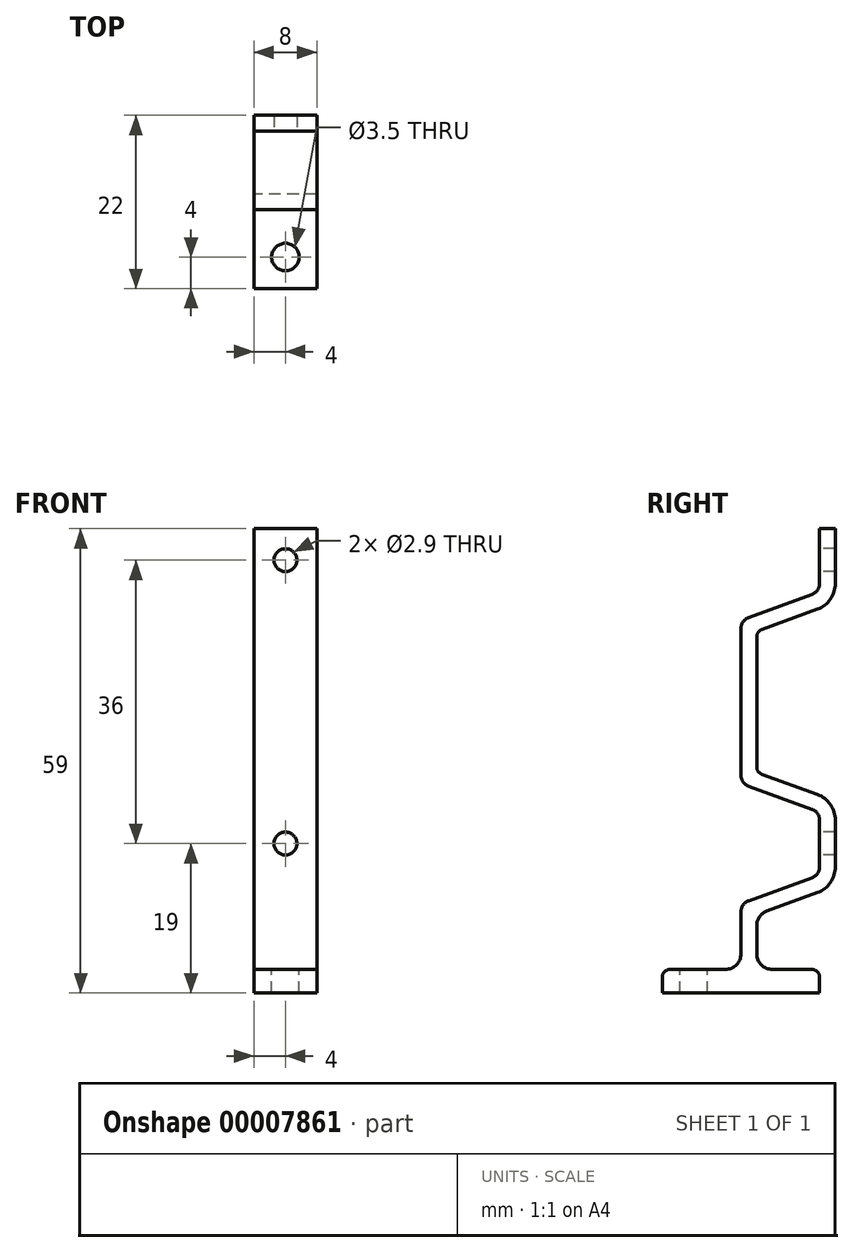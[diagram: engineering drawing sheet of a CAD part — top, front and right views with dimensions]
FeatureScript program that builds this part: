
annotation { "Feature Type Name" : "Feature", "Feature Type Description" : "" }
export const myFeature = defineFeature(function(context is Context, id is Id, definition is map)
    precondition{}
    {
        {
            var Q0;
            Q0=qCreatedBy(makeId("Front.planeOp"),FACE);
            var sketch = newSketch(context, id + "F0", { "sketchPlane" : qUnion([Q0])});
            skPoint(sketch, "E0.rect.middle", {"position": v(0, 0) * mm});
            skCircle(sketch, "E1", {"center": v(0, 52) * mm, "radius": 1.45 * mm});
            skCircle(sketch, "E2", {"center": v(0, 16) * mm, "radius": 1.45 * mm});
            skSolve(sketch);
        }
        {
            var Q0;
            Q0=qCreatedBy(makeId("Right.planeOp"),FACE);
            var sketch = newSketch(context, id + "F1", { "sketchPlane" : qUnion([Q0])});
            skLineSegment(sketch, "E3", {"start": v(0, 2) * mm, "end": v(0, 7.3) * mm});
            skLineSegment(sketch, "E4", {"start": v(0.99, 8.72) * mm, "end": v(9.01, 11.64) * mm});
            skLineSegment(sketch, "E5", {"start": v(10, 13.05) * mm, "end": v(10, 18.95) * mm});
            skLineSegment(sketch, "E6", {"start": v(9.01, 20.36) * mm, "end": v(0.99, 23.28) * mm});
            skLineSegment(sketch, "E7", {"start": v(0, 24.7) * mm, "end": v(0, 43.3) * mm});
            skLineSegment(sketch, "E8", {"start": v(0.99, 44.72) * mm, "end": v(9.01, 47.64) * mm});
            skLineSegment(sketch, "E9", {"start": v(10, 49.05) * mm, "end": v(10, 56) * mm});
            skLineSegment(sketch, "E10", {"start": v(10, 16) * mm, "end": v(0, 16) * mm, "construction": true});
            skLineSegment(sketch, "E11", {"start": v(10, 52) * mm, "end": v(0, 52) * mm, "construction": true});
            skLineSegment(sketch, "E12.bottom", {"start": v(-9, 0) * mm, "end": v(-2, 0) * mm});
            skLineSegment(sketch, "E12.top", {"start": v(-10, -3) * mm, "end": v(10, -3) * mm});
            skLineSegment(sketch, "E12.left", {"start": v(-10, -1) * mm, "end": v(-10, -3) * mm});
            skLineSegment(sketch, "E12.right", {"start": v(10, -1) * mm, "end": v(10, -3) * mm});
            skPoint(sketch, "E13.visualSharp", {"position": v(10, 48) * mm});
            skArc(sketch, "E13.filletArc", {"start": v(9.01, 47.64) * mm, "mid": v(9.73, 48.19) * mm, "end": v(10, 49.05) * mm});
            skPoint(sketch, "E14.visualSharp", {"position": v(0, 44.36) * mm});
            skArc(sketch, "E14.filletArc", {"start": v(0.99, 44.72) * mm, "mid": v(0.27, 44.17) * mm, "end": v(0, 43.3) * mm});
            skPoint(sketch, "E15.visualSharp", {"position": v(0, 23.64) * mm});
            skArc(sketch, "E15.filletArc", {"start": v(0, 24.7) * mm, "mid": v(0.27, 23.83) * mm, "end": v(0.99, 23.28) * mm});
            skPoint(sketch, "E16.visualSharp", {"position": v(10, 20) * mm});
            skArc(sketch, "E16.filletArc", {"start": v(10, 18.95) * mm, "mid": v(9.73, 19.81) * mm, "end": v(9.01, 20.36) * mm});
            skPoint(sketch, "E17.visualSharp", {"position": v(10, 12) * mm});
            skArc(sketch, "E17.filletArc", {"start": v(9.01, 11.64) * mm, "mid": v(9.73, 12.19) * mm, "end": v(10, 13.05) * mm});
            skPoint(sketch, "E18.visualSharp", {"position": v(0, 8.36) * mm});
            skArc(sketch, "E18.filletArc", {"start": v(0.99, 8.72) * mm, "mid": v(0.27, 8.17) * mm, "end": v(0, 7.3) * mm});
            skLineSegment(sketch, "E19.0", {"start": v(12, 49.05) * mm, "end": v(12, 56) * mm});
            skArc(sketch, "E19.1", {"start": v(9.7, 45.76) * mm, "mid": v(11.37, 47.04) * mm, "end": v(12, 49.05) * mm});
            skLineSegment(sketch, "E19.2", {"start": v(2.66, 43.2) * mm, "end": v(9.7, 45.76) * mm});
            skLineSegment(sketch, "E19.3", {"start": v(2, 25.74) * mm, "end": v(2, 42.26) * mm});
            skLineSegment(sketch, "E19.4", {"start": v(9.7, 22.24) * mm, "end": v(2.66, 24.8) * mm});
            skArc(sketch, "E19.5", {"start": v(12, 18.95) * mm, "mid": v(11.37, 20.96) * mm, "end": v(9.7, 22.24) * mm});
            skLineSegment(sketch, "E19.6", {"start": v(12, 13.05) * mm, "end": v(12, 18.95) * mm});
            skArc(sketch, "E19.7", {"start": v(9.7, 9.76) * mm, "mid": v(11.37, 11.04) * mm, "end": v(12, 13.05) * mm});
            skLineSegment(sketch, "E19.8", {"start": v(3.32, 7.44) * mm, "end": v(9.7, 9.76) * mm});
            skLineSegment(sketch, "E19.9", {"start": v(2, 2) * mm, "end": v(2, 5.56) * mm});
            skLineSegment(sketch, "E20", {"start": v(10, 56) * mm, "end": v(12, 56) * mm});
            skLineSegment(sketch, "E21.trimOffspring", {"start": v(4, 0) * mm, "end": v(9, 0) * mm});
            skPoint(sketch, "E22.visualSharp", {"position": v(0, 0) * mm});
            skArc(sketch, "E22.filletArc", {"start": v(-2, 0) * mm, "mid": v(-0.59, 0.59) * mm, "end": v(0, 2) * mm});
            skPoint(sketch, "E23.visualSharp", {"position": v(2, 0) * mm});
            skArc(sketch, "E23.filletArc", {"start": v(2, 2) * mm, "mid": v(2.59, 0.59) * mm, "end": v(4, 0) * mm});
            skPoint(sketch, "E24.visualSharp", {"position": v(2, 6.96) * mm});
            skArc(sketch, "E24.filletArc", {"start": v(3.32, 7.44) * mm, "mid": v(2.36, 6.7) * mm, "end": v(2, 5.56) * mm});
            skPoint(sketch, "E25.visualSharp", {"position": v(2, 25.04) * mm});
            skArc(sketch, "E25.filletArc", {"start": v(2, 25.74) * mm, "mid": v(2.18, 25.17) * mm, "end": v(2.66, 24.8) * mm});
            skPoint(sketch, "E26.visualSharp", {"position": v(2, 42.96) * mm});
            skArc(sketch, "E26.filletArc", {"start": v(2.66, 43.2) * mm, "mid": v(2.18, 42.83) * mm, "end": v(2, 42.26) * mm});
            skPoint(sketch, "E27.visualSharp", {"position": v(-10, 0) * mm});
            skArc(sketch, "E27.filletArc", {"start": v(-9, 0) * mm, "mid": v(-9.7, -0.3) * mm, "end": v(-10, -1) * mm});
            skPoint(sketch, "E28.visualSharp", {"position": v(10, 0) * mm});
            skArc(sketch, "E28.filletArc", {"start": v(10, -1) * mm, "mid": v(9.7, -0.3) * mm, "end": v(9, 0) * mm});
            skSolve(sketch);
        }
        {
            var Q0;
            Q0 = qSketchRegion(id + "F1", true);
            extrude(context, id + "F2", {"entities" : qUnion([Q0]), "depth" : 4 * mm});
        }
        {
            var Q0;
            Q0 = qSketchRegion(id + "F1", true);
            extrude(context, id + "F3", {"entities" : qUnion([Q0]), "operationType" : NewBodyOperationType.ADD, "oppositeDirection" : true, "depth" : 4 * mm});
        }
        {
            var Q0;
            Q0 = qSketchRegion(id + "F0", true);
            extrude(context, id + "F4", {"entities" : qUnion([Q0]), "operationType" : NewBodyOperationType.REMOVE, "endBound" : BoundingType.THROUGH_ALL, "oppositeDirection" : true, "depth" : 25 * mm});
        }
        {
            var Q0;
            {var subQ0=sQuery(id+"F1.wireOp",EDGE,"E12.bottom");Q0=makeQuery(id+"F3.boolean.opBoolean","MERGE",FACE,{"derivedFrom":[makeQuery(id+"F2.opExtrude","SWEPT_FACE",FACE,{"disambiguationData":[OSD([subQ0])]}),makeQuery(id+"F3.opExtrude","SWEPT_FACE",FACE,{"disambiguationData":[OSD([subQ0])]})]});}
            var sketch = newSketch(context, id + "F5", { "sketchPlane" : qUnion([Q0])});
            skCircle(sketch, "E29", {"center": v(0, -6) * mm, "radius": 1.75 * mm});
            skSolve(sketch);
        }
        {
            var Q0;
            Q0 = qSketchRegion(id + "F5", true);
            extrude(context, id + "F6", {"entities" : qUnion([Q0]), "operationType" : NewBodyOperationType.REMOVE, "oppositeDirection" : true, "depth" : 25 * mm});
        }
    });
